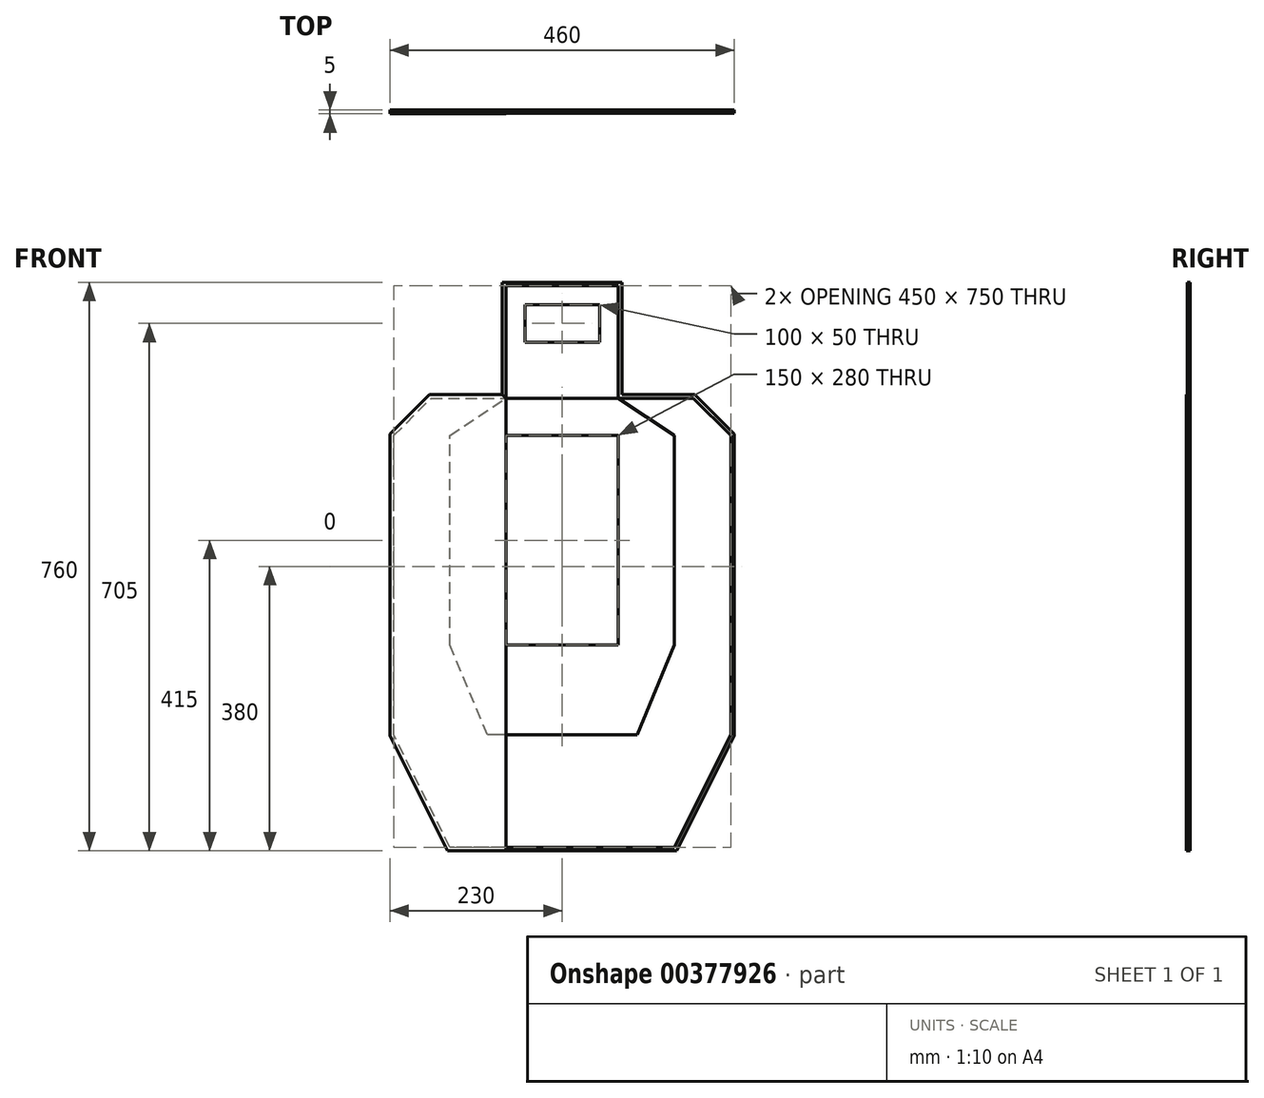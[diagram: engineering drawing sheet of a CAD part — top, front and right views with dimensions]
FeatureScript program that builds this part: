
annotation { "Feature Type Name" : "Feature", "Feature Type Description" : "" }
export const myFeature = defineFeature(function(context is Context, id is Id, definition is map)
    precondition{}
    {
        {
            var Q0;
            Q0=qCreatedBy(makeId("Front.planeOp"),FACE);
            var sketch = newSketch(context, id + "F0", { "sketchPlane" : qUnion([Q0])});
            skLineSegment(sketch, "E0.bottom", {"start": v(0, 100) * mm, "end": v(50, 100) * mm, "construction": true});
            skLineSegment(sketch, "E0.top", {"start": v(0, 125) * mm, "end": v(50, 125) * mm});
            skLineSegment(sketch, "E0.right", {"start": v(50, 100) * mm, "end": v(50, 125) * mm});
            skLineSegment(sketch, "E1.MirrorCS", {"start": v(0, 75) * mm, "end": v(50, 75) * mm});
            skLineSegment(sketch, "E2.MirrorCS", {"start": v(50, 100) * mm, "end": v(50, 75) * mm});
            skLineSegment(sketch, "E3.MirrorCS", {"start": v(0, 0) * mm, "end": v(0, 100) * mm, "construction": true});
            skLineSegment(sketch, "E4.MirrorCS", {"start": v(0, 125) * mm, "end": v(-50, 125) * mm});
            skLineSegment(sketch, "E5.MirrorCS", {"start": v(-50, 100) * mm, "end": v(-50, 125) * mm});
            skLineSegment(sketch, "E6.MirrorCS", {"start": v(-50, 100) * mm, "end": v(-50, 75) * mm});
            skLineSegment(sketch, "E7.MirrorCS", {"start": v(0, 75) * mm, "end": v(-50, 75) * mm});
            skSolve(sketch);
        }
        {
            var Q0;
            Q0=qSketchRegion(id+"F0",true);
            extrude(context, id + "F1", {"entities" : qUnion([Q0]), "oppositeDirection" : true, "depth" : 3 * mm});
        }
        {
            var Q0;
            Q0=qCreatedBy(makeId("Front.planeOp"),FACE);
            var sketch = newSketch(context, id + "F2", { "sketchPlane" : qUnion([Q0])});
            skLineSegment(sketch, "E8", {"start": v(75, 0) * mm, "end": v(75, 150) * mm});
            skLineSegment(sketch, "E9", {"start": v(75, 150) * mm, "end": v(-75, 150) * mm});
            skLineSegment(sketch, "E10", {"start": v(-75, 150) * mm, "end": v(-75, 0) * mm});
            skLineSegment(sketch, "E11", {"start": v(-75, 0) * mm, "end": v(75, 0) * mm});
            skLineSegment(sketch, "E12.0", {"start": v(0, 125) * mm, "end": v(-50, 125) * mm});
            skLineSegment(sketch, "E13.0", {"start": v(0, 125) * mm, "end": v(50, 125) * mm});
            skLineSegment(sketch, "E14.0", {"start": v(50, 100) * mm, "end": v(50, 125) * mm});
            skLineSegment(sketch, "E15.1", {"start": v(50, 100) * mm, "end": v(50, 75) * mm});
            skLineSegment(sketch, "E16.0", {"start": v(0, 75) * mm, "end": v(50, 75) * mm});
            skLineSegment(sketch, "E17.0", {"start": v(0, 75) * mm, "end": v(-50, 75) * mm});
            skLineSegment(sketch, "E18.0", {"start": v(-50, 100) * mm, "end": v(-50, 75) * mm});
            skLineSegment(sketch, "E19.1", {"start": v(-50, 100) * mm, "end": v(-50, 125) * mm});
            skLineSegment(sketch, "E20", {"start": v(0, 125) * mm, "end": v(0, 150) * mm, "construction": true});
            skLineSegment(sketch, "E21", {"start": v(0, 150) * mm, "end": v(0, 137.5) * mm, "construction": true});
            skSolve(sketch);
        }
        {
            var Q0;
            {var subQ0=sQuery(id+"F2.wireOp",EDGE,"E8");Q0=makeQuery(id+"F2.imprint","IMPRINT",FACE,{"disambiguationData":[TD([[makeQuery(id+"F2.imprint","IMPRINT",EDGE,{"derivedFrom":subQ0}),1.0]])]});}
            extrude(context, id + "F3", {"entities" : qUnion([Q0]), "oppositeDirection" : true, "depth" : 3 * mm});
        }
        {
            var Q0;
            Q0=qCreatedBy(makeId("Front.planeOp"),FACE);
            var sketch = newSketch(context, id + "F4", { "sketchPlane" : qUnion([Q0])});
            skLineSegment(sketch, "E22.bottom", {"start": v(75, -50) * mm, "end": v(-75, -50) * mm});
            skLineSegment(sketch, "E22.top", {"start": v(75, -330) * mm, "end": v(-75, -330) * mm});
            skLineSegment(sketch, "E22.left", {"start": v(75, -50) * mm, "end": v(75, -330) * mm});
            skLineSegment(sketch, "E22.right", {"start": v(-75, -50) * mm, "end": v(-75, -330) * mm});
            skLineSegment(sketch, "E23", {"start": v(0, 0) * mm, "end": v(0, -50) * mm, "construction": true});
            skLineSegment(sketch, "E24.0", {"start": v(-75, 0) * mm, "end": v(75, 0) * mm, "construction": true});
            skLineSegment(sketch, "E25", {"start": v(75, 0) * mm, "end": v(75, -50) * mm, "construction": true});
            skSolve(sketch);
        }
        {
            var Q0;
            Q0=makeQuery(id+"F4.imprint","IMPRINT",FACE,{"disambiguationData":[TD([[makeQuery(id+"F4.imprint","IMPRINT",EDGE,{"derivedFrom":sQuery(id+"F4.wireOp",EDGE,"E22.bottom")}),1.0]])]});
            extrude(context, id + "F5", {"entities" : qUnion([Q0]), "oppositeDirection" : true, "depth" : 3 * mm});
        }
        {
            var Q0;
            Q0=qCreatedBy(makeId("Front.planeOp"),FACE);
            var sketch = newSketch(context, id + "F6", { "sketchPlane" : qUnion([Q0])});
            skLineSegment(sketch, "E26.0", {"start": v(-75, 0) * mm, "end": v(75, 0) * mm});
            skLineSegment(sketch, "E27.1", {"start": v(75, -50) * mm, "end": v(75, -330) * mm});
            skLineSegment(sketch, "E28.2", {"start": v(75, -50) * mm, "end": v(-75, -50) * mm});
            skLineSegment(sketch, "E29.3", {"start": v(-75, -50) * mm, "end": v(-75, -330) * mm});
            skLineSegment(sketch, "E30.0", {"start": v(75, -330) * mm, "end": v(-75, -330) * mm});
            skLineSegment(sketch, "E31", {"start": v(75, 0) * mm, "end": v(150, -50) * mm});
            skLineSegment(sketch, "E32", {"start": v(150, -50) * mm, "end": v(150, -330) * mm});
            skLineSegment(sketch, "E33", {"start": v(150, -330) * mm, "end": v(100, -450) * mm});
            skLineSegment(sketch, "E34", {"start": v(100, -450) * mm, "end": v(-100, -450) * mm});
            skLineSegment(sketch, "E35", {"start": v(-100, -450) * mm, "end": v(-150, -330) * mm});
            skLineSegment(sketch, "E36", {"start": v(-150, -330) * mm, "end": v(-150, -50) * mm});
            skLineSegment(sketch, "E37", {"start": v(-150, -50) * mm, "end": v(-75, 0) * mm});
            skLineSegment(sketch, "E38", {"start": v(0, -450) * mm, "end": v(0, -50) * mm, "construction": true});
            skLineSegment(sketch, "E39", {"start": v(150, -50) * mm, "end": v(75, -50) * mm, "construction": true});
            skLineSegment(sketch, "E40", {"start": v(-55.04, -50) * mm, "end": v(-150, -50) * mm, "construction": true});
            skLineSegment(sketch, "E41", {"start": v(150, -330) * mm, "end": v(150, -450) * mm, "construction": true});
            skLineSegment(sketch, "E42", {"start": v(100, -450) * mm, "end": v(150, -450) * mm, "construction": true});
            skLineSegment(sketch, "E43", {"start": v(150, -330) * mm, "end": v(-150, -330) * mm, "construction": true});
            skLineSegment(sketch, "E44", {"start": v(-150, -330) * mm, "end": v(-150, -450) * mm, "construction": true});
            skLineSegment(sketch, "E45", {"start": v(-150, -450) * mm, "end": v(-100, -450) * mm, "construction": true});
            skSolve(sketch);
        }
        {
            var Q0;
            Q0=makeQuery(id+"F6.imprint","IMPRINT",FACE,{"disambiguationData":[TD([[makeQuery(id+"F6.imprint","IMPRINT",EDGE,{"derivedFrom":sQuery(id+"F6.wireOp",EDGE,"E26.0")}),-1.0]])]});
            extrude(context, id + "F7", {"entities" : qUnion([Q0]), "oppositeDirection" : true, "depth" : 3 * mm});
        }
        {
            var Q0;
            Q0=makeQuery(id+"F7.opExtrude","CAP_FACE",FACE,{"disambiguationData":[OSD([sQuery(id+"F6.wireOp",EDGE,"E26.0"),sQuery(id+"F6.wireOp",EDGE,"E27.1"),sQuery(id+"F6.wireOp",EDGE,"E28.2"),sQuery(id+"F6.wireOp",EDGE,"E29.3"),sQuery(id+"F6.wireOp",EDGE,"E30.0"),sQuery(id+"F6.wireOp",EDGE,"E31"),sQuery(id+"F6.wireOp",EDGE,"E32"),sQuery(id+"F6.wireOp",EDGE,"E33"),sQuery(id+"F6.wireOp",EDGE,"E34"),sQuery(id+"F6.wireOp",EDGE,"E35"),sQuery(id+"F6.wireOp",EDGE,"E36"),sQuery(id+"F6.wireOp",EDGE,"E37")])],"isStart":true});
            var sketch = newSketch(context, id + "F8", { "sketchPlane" : qUnion([Q0])});
            skLineSegment(sketch, "E46.0", {"start": v(75, 0) * mm, "end": v(150, -50) * mm});
            skLineSegment(sketch, "E47.0", {"start": v(150, -50) * mm, "end": v(150, -330) * mm});
            skLineSegment(sketch, "E48.0", {"start": v(150, -330) * mm, "end": v(100, -450) * mm});
            skLineSegment(sketch, "E49.1", {"start": v(100, -450) * mm, "end": v(-100, -450) * mm});
            skLineSegment(sketch, "E50.0", {"start": v(-150, -330) * mm, "end": v(-150, -50) * mm});
            skLineSegment(sketch, "E51.0", {"start": v(-100, -450) * mm, "end": v(-150, -330) * mm});
            skLineSegment(sketch, "E52.0", {"start": v(-150, -50) * mm, "end": v(-75, 0) * mm});
            skLineSegment(sketch, "E53", {"start": v(75, 0) * mm, "end": v(175, 0) * mm});
            skLineSegment(sketch, "E54", {"start": v(175, 0) * mm, "end": v(225, -50) * mm});
            skLineSegment(sketch, "E55", {"start": v(225, -50) * mm, "end": v(225, -450) * mm});
            skLineSegment(sketch, "E56", {"start": v(225, -450) * mm, "end": v(150, -600) * mm});
            skLineSegment(sketch, "E57", {"start": v(150, -600) * mm, "end": v(-150, -600) * mm});
            skLineSegment(sketch, "E58", {"start": v(-150, -600) * mm, "end": v(-225, -450) * mm});
            skLineSegment(sketch, "E59", {"start": v(-225, -450) * mm, "end": v(-225, -50) * mm});
            skLineSegment(sketch, "E60", {"start": v(-225, -50) * mm, "end": v(-175, 0) * mm});
            skLineSegment(sketch, "E61", {"start": v(-175, 0) * mm, "end": v(-75, 0) * mm});
            skLineSegment(sketch, "E62", {"start": v(225, -50) * mm, "end": v(225, 0) * mm, "construction": true});
            skLineSegment(sketch, "E63", {"start": v(225, 0) * mm, "end": v(175, 0) * mm, "construction": true});
            skLineSegment(sketch, "E64", {"start": v(225, -450) * mm, "end": v(225, -600) * mm, "construction": true});
            skLineSegment(sketch, "E65", {"start": v(225, -600) * mm, "end": v(150, -600) * mm, "construction": true});
            skLineSegment(sketch, "E66", {"start": v(-225, -450) * mm, "end": v(-225, -600) * mm, "construction": true});
            skLineSegment(sketch, "E67", {"start": v(-225, -600) * mm, "end": v(-150, -600) * mm, "construction": true});
            skLineSegment(sketch, "E68", {"start": v(-175, 0) * mm, "end": v(-225, 0) * mm, "construction": true});
            skLineSegment(sketch, "E69", {"start": v(-225, 0) * mm, "end": v(-225, -50) * mm, "construction": true});
            skSolve(sketch);
        }
        {
            var Q0;
            Q0=qSketchRegion(id+"F8",true);
            extrude(context, id + "F9", {"entities" : qUnion([Q0]), "oppositeDirection" : true, "depth" : 3 * mm});
        }
        {
            var Q0;
            Q0=makeQuery(id+"F9.opExtrude","CAP_FACE",FACE,{"disambiguationData":[OSD([sQuery(id+"F8.wireOp",EDGE,"E46.0"),sQuery(id+"F8.wireOp",EDGE,"E47.0"),sQuery(id+"F8.wireOp",EDGE,"E48.0"),sQuery(id+"F8.wireOp",EDGE,"E49.1"),sQuery(id+"F8.wireOp",EDGE,"E50.0"),sQuery(id+"F8.wireOp",EDGE,"E51.0"),sQuery(id+"F8.wireOp",EDGE,"E52.0"),sQuery(id+"F8.wireOp",EDGE,"E53"),sQuery(id+"F8.wireOp",EDGE,"E54"),sQuery(id+"F8.wireOp",EDGE,"E55"),sQuery(id+"F8.wireOp",EDGE,"E56"),sQuery(id+"F8.wireOp",EDGE,"E57"),sQuery(id+"F8.wireOp",EDGE,"E58"),sQuery(id+"F8.wireOp",EDGE,"E59"),sQuery(id+"F8.wireOp",EDGE,"E60"),sQuery(id+"F8.wireOp",EDGE,"E61")])],"isStart":true});
            var sketch = newSketch(context, id + "F10", { "sketchPlane" : qUnion([Q0])});
            skLineSegment(sketch, "E70.0", {"start": v(75, 150) * mm, "end": v(-75, 150) * mm});
            skLineSegment(sketch, "E71.0", {"start": v(75, 0) * mm, "end": v(75, 150) * mm});
            skLineSegment(sketch, "E72.1", {"start": v(75, 0) * mm, "end": v(175, 0) * mm});
            skLineSegment(sketch, "E73.0", {"start": v(175, 0) * mm, "end": v(225, -50) * mm});
            skLineSegment(sketch, "E74.1", {"start": v(225, -50) * mm, "end": v(225, -450) * mm});
            skLineSegment(sketch, "E75.0", {"start": v(225, -450) * mm, "end": v(150, -600) * mm});
            skLineSegment(sketch, "E76.1", {"start": v(150, -600) * mm, "end": v(-150, -600) * mm});
            skLineSegment(sketch, "E77.2", {"start": v(-150, -600) * mm, "end": v(-225, -450) * mm});
            skLineSegment(sketch, "E78.3", {"start": v(-225, -450) * mm, "end": v(-225, -50) * mm});
            skLineSegment(sketch, "E79.4", {"start": v(-225, -50) * mm, "end": v(-175, 0) * mm});
            skLineSegment(sketch, "E80.5", {"start": v(-175, 0) * mm, "end": v(-75, 0) * mm});
            skLineSegment(sketch, "E81.0", {"start": v(-75, 150) * mm, "end": v(-75, 0) * mm});
            skLineSegment(sketch, "E82.0", {"start": v(177.07, 5) * mm, "end": v(230, -47.93) * mm});
            skLineSegment(sketch, "E82.1", {"start": v(-230, -451.18) * mm, "end": v(-230, -47.93) * mm});
            skLineSegment(sketch, "E82.2", {"start": v(-153.1, -605) * mm, "end": v(-230, -451.18) * mm});
            skLineSegment(sketch, "E82.3", {"start": v(153.1, -605) * mm, "end": v(-153.1, -605) * mm});
            skLineSegment(sketch, "E82.4", {"start": v(230, -451.18) * mm, "end": v(153.1, -605) * mm});
            skLineSegment(sketch, "E82.5", {"start": v(-230, -47.93) * mm, "end": v(-177.07, 5) * mm});
            skLineSegment(sketch, "E82.6", {"start": v(230, -47.93) * mm, "end": v(230, -451.18) * mm});
            skLineSegment(sketch, "E82.7", {"start": v(-177.07, 5) * mm, "end": v(-80, 5) * mm});
            skLineSegment(sketch, "E82.8", {"start": v(-80, 155) * mm, "end": v(-80, 5) * mm});
            skLineSegment(sketch, "E82.9", {"start": v(80, 155) * mm, "end": v(-80, 155) * mm});
            skLineSegment(sketch, "E82.10", {"start": v(80, 5) * mm, "end": v(80, 155) * mm});
            skLineSegment(sketch, "E82.11", {"start": v(80, 5) * mm, "end": v(177.07, 5) * mm});
            skSolve(sketch);
        }
        {
            var Q0;
            Q0=makeQuery(id+"F10.imprint","IMPRINT",FACE,{"disambiguationData":[TD([[makeQuery(id+"F10.imprint","IMPRINT",EDGE,{"derivedFrom":sQuery(id+"F10.wireOp",EDGE,"E70.0")}),-1.0]])]});
            extrude(context, id + "F11", {"entities" : qUnion([Q0]), "oppositeDirection" : true, "depth" : 3 * mm});
        }
        {
            var Q0;
            Q0=makeQuery(id+"F9.opExtrude","CAP_FACE",FACE,{"disambiguationData":[OSD([sQuery(id+"F8.wireOp",EDGE,"E46.0"),sQuery(id+"F8.wireOp",EDGE,"E47.0"),sQuery(id+"F8.wireOp",EDGE,"E48.0"),sQuery(id+"F8.wireOp",EDGE,"E49.1"),sQuery(id+"F8.wireOp",EDGE,"E50.0"),sQuery(id+"F8.wireOp",EDGE,"E51.0"),sQuery(id+"F8.wireOp",EDGE,"E52.0"),sQuery(id+"F8.wireOp",EDGE,"E53"),sQuery(id+"F8.wireOp",EDGE,"E54"),sQuery(id+"F8.wireOp",EDGE,"E55"),sQuery(id+"F8.wireOp",EDGE,"E56"),sQuery(id+"F8.wireOp",EDGE,"E57"),sQuery(id+"F8.wireOp",EDGE,"E58"),sQuery(id+"F8.wireOp",EDGE,"E59"),sQuery(id+"F8.wireOp",EDGE,"E60"),sQuery(id+"F8.wireOp",EDGE,"E61")])],"isStart":false});
            var sketch = newSketch(context, id + "F12", { "sketchPlane" : qUnion([Q0])});
            skLineSegment(sketch, "E83.0", {"start": v(75, 150) * mm, "end": v(75, 0) * mm});
            skLineSegment(sketch, "E84.0", {"start": v(175, 0) * mm, "end": v(75, 0) * mm});
            skLineSegment(sketch, "E85.0", {"start": v(-75, 150) * mm, "end": v(75, 150) * mm});
            skLineSegment(sketch, "E86.0", {"start": v(225, -50) * mm, "end": v(175, 0) * mm});
            skLineSegment(sketch, "E87.0", {"start": v(-225, -50) * mm, "end": v(-225, -450) * mm});
            skLineSegment(sketch, "E87.1", {"start": v(225, -450) * mm, "end": v(225, -50) * mm});
            skLineSegment(sketch, "E87.2", {"start": v(150, -600) * mm, "end": v(225, -450) * mm});
            skLineSegment(sketch, "E87.3", {"start": v(-225, -450) * mm, "end": v(-150, -600) * mm});
            skLineSegment(sketch, "E87.4", {"start": v(-150, -600) * mm, "end": v(150, -600) * mm});
            skLineSegment(sketch, "E88.0", {"start": v(-175, 0) * mm, "end": v(-225, -50) * mm});
            skLineSegment(sketch, "E89.0", {"start": v(-75, 0) * mm, "end": v(-175, 0) * mm});
            skLineSegment(sketch, "E90.0", {"start": v(-75, 0) * mm, "end": v(-75, 150) * mm});
            skSolve(sketch);
        }
        {
            var Q0;
            Q0=qSketchRegion(id+"F12",true);
            extrude(context, id + "F13", {"entities" : qUnion([Q0]), "depth" : 1 * mm});
        }
        {
            var Q0;
            Q0=makeQuery(id+"F13.opExtrude","CAP_FACE",FACE,{"disambiguationData":[OSD([sQuery(id+"F12.wireOp",EDGE,"E83.0"),sQuery(id+"F12.wireOp",EDGE,"E84.0"),sQuery(id+"F12.wireOp",EDGE,"E85.0"),sQuery(id+"F12.wireOp",EDGE,"E86.0"),sQuery(id+"F12.wireOp",EDGE,"E87.0"),sQuery(id+"F12.wireOp",EDGE,"E87.1"),sQuery(id+"F12.wireOp",EDGE,"E87.2"),sQuery(id+"F12.wireOp",EDGE,"E87.3"),sQuery(id+"F12.wireOp",EDGE,"E87.4"),sQuery(id+"F12.wireOp",EDGE,"E88.0"),sQuery(id+"F12.wireOp",EDGE,"E89.0"),sQuery(id+"F12.wireOp",EDGE,"E90.0")])],"isStart":false});
            var sketch = newSketch(context, id + "F14", { "sketchPlane" : qUnion([Q0])});
            skLineSegment(sketch, "E91.0", {"start": v(-80, 155) * mm, "end": v(80, 155) * mm});
            skLineSegment(sketch, "E92.0", {"start": v(80, 155) * mm, "end": v(80, 5) * mm});
            skLineSegment(sketch, "E93.0", {"start": v(-80, 5) * mm, "end": v(-80, 155) * mm});
            skLineSegment(sketch, "E94.0", {"start": v(177.07, 5) * mm, "end": v(80, 5) * mm});
            skLineSegment(sketch, "E95.0", {"start": v(-80, 5) * mm, "end": v(-177.07, 5) * mm});
            skLineSegment(sketch, "E96.0", {"start": v(230, -47.93) * mm, "end": v(177.07, 5) * mm});
            skLineSegment(sketch, "E97.0", {"start": v(-177.07, 5) * mm, "end": v(-230, -47.93) * mm});
            skLineSegment(sketch, "E98.1", {"start": v(-230, -47.93) * mm, "end": v(-230, -451.18) * mm});
            skLineSegment(sketch, "E99.0", {"start": v(-230, -451.18) * mm, "end": v(-153.1, -605) * mm});
            skLineSegment(sketch, "E100.0", {"start": v(-153.1, -605) * mm, "end": v(153.1, -605) * mm});
            skLineSegment(sketch, "E101.0", {"start": v(153.1, -605) * mm, "end": v(230, -451.18) * mm});
            skLineSegment(sketch, "E102.0", {"start": v(230, -451.18) * mm, "end": v(230, -47.93) * mm});
            skLineSegment(sketch, "E103.0", {"start": v(-75, 150) * mm, "end": v(75, 150) * mm});
            skLineSegment(sketch, "E104.0", {"start": v(-75, 0) * mm, "end": v(-75, 150) * mm});
            skLineSegment(sketch, "E105.0", {"start": v(75, 150) * mm, "end": v(75, 0) * mm});
            skLineSegment(sketch, "E106.0", {"start": v(175, 0) * mm, "end": v(75, 0) * mm});
            skLineSegment(sketch, "E107.0", {"start": v(225, -50) * mm, "end": v(175, 0) * mm});
            skLineSegment(sketch, "E108.0", {"start": v(150, -600) * mm, "end": v(225, -450) * mm});
            skLineSegment(sketch, "E109.0", {"start": v(225, -450) * mm, "end": v(225, -50) * mm});
            skLineSegment(sketch, "E110.0", {"start": v(-150, -600) * mm, "end": v(150, -600) * mm});
            skLineSegment(sketch, "E111.0", {"start": v(-225, -450) * mm, "end": v(-150, -600) * mm});
            skLineSegment(sketch, "E112.0", {"start": v(-225, -50) * mm, "end": v(-225, -450) * mm});
            skLineSegment(sketch, "E113.0", {"start": v(-175, 0) * mm, "end": v(-225, -50) * mm});
            skLineSegment(sketch, "E114.0", {"start": v(-75, 0) * mm, "end": v(-175, 0) * mm});
            skSolve(sketch);
        }
        {
            var Q0;
            Q0=makeQuery(id+"F14.imprint","IMPRINT",FACE,{"disambiguationData":[TD([[makeQuery(id+"F14.imprint","IMPRINT",EDGE,{"derivedFrom":sQuery(id+"F14.wireOp",EDGE,"E91.0")}),-1.0]])]});
            extrude(context, id + "F15", {"entities" : qUnion([Q0]), "oppositeDirection" : true, "depth" : 1 * mm});
        }
        {
            var Q0;
            Q0=makeQuery(id+"F9.opExtrude","CAP_FACE",FACE,{"disambiguationData":[OSD([sQuery(id+"F8.wireOp",EDGE,"E46.0"),sQuery(id+"F8.wireOp",EDGE,"E47.0"),sQuery(id+"F8.wireOp",EDGE,"E48.0"),sQuery(id+"F8.wireOp",EDGE,"E49.1"),sQuery(id+"F8.wireOp",EDGE,"E50.0"),sQuery(id+"F8.wireOp",EDGE,"E51.0"),sQuery(id+"F8.wireOp",EDGE,"E52.0"),sQuery(id+"F8.wireOp",EDGE,"E53"),sQuery(id+"F8.wireOp",EDGE,"E54"),sQuery(id+"F8.wireOp",EDGE,"E55"),sQuery(id+"F8.wireOp",EDGE,"E56"),sQuery(id+"F8.wireOp",EDGE,"E57"),sQuery(id+"F8.wireOp",EDGE,"E58"),sQuery(id+"F8.wireOp",EDGE,"E59"),sQuery(id+"F8.wireOp",EDGE,"E60"),sQuery(id+"F8.wireOp",EDGE,"E61")])],"isStart":true});
            var sketch = newSketch(context, id + "F16", { "sketchPlane" : qUnion([Q0])});
            skLineSegment(sketch, "E115.0", {"start": v(-75, -605) * mm, "end": v(-153.1, -605) * mm});
            skLineSegment(sketch, "E116.0", {"start": v(-153.1, -605) * mm, "end": v(-230, -451.18) * mm});
            skLineSegment(sketch, "E117.0", {"start": v(-230, -451.18) * mm, "end": v(-230, -47.93) * mm});
            skLineSegment(sketch, "E118.0", {"start": v(-230, -47.93) * mm, "end": v(-177.07, 5) * mm});
            skLineSegment(sketch, "E119.0", {"start": v(-177.07, 5) * mm, "end": v(-80, 5) * mm});
            skLineSegment(sketch, "E120.0", {"start": v(-75, 0) * mm, "end": v(75, 0) * mm, "construction": true});
            skLineSegment(sketch, "E121", {"start": v(-80, 5) * mm, "end": v(-75, 0) * mm});
            skLineSegment(sketch, "E122", {"start": v(-75, 0) * mm, "end": v(-75, -605) * mm});
            skLineSegment(sketch, "E123", {"start": v(-75, -605) * mm, "end": v(-75, 0) * mm});
            skSolve(sketch);
        }
        {
            var Q0;
            Q0 = qSketchRegion(id + "F16", true);
            extrude(context, id + "F17", {"entities" : qUnion([Q0]), "depth" : 1 * mm});
        }
    });
